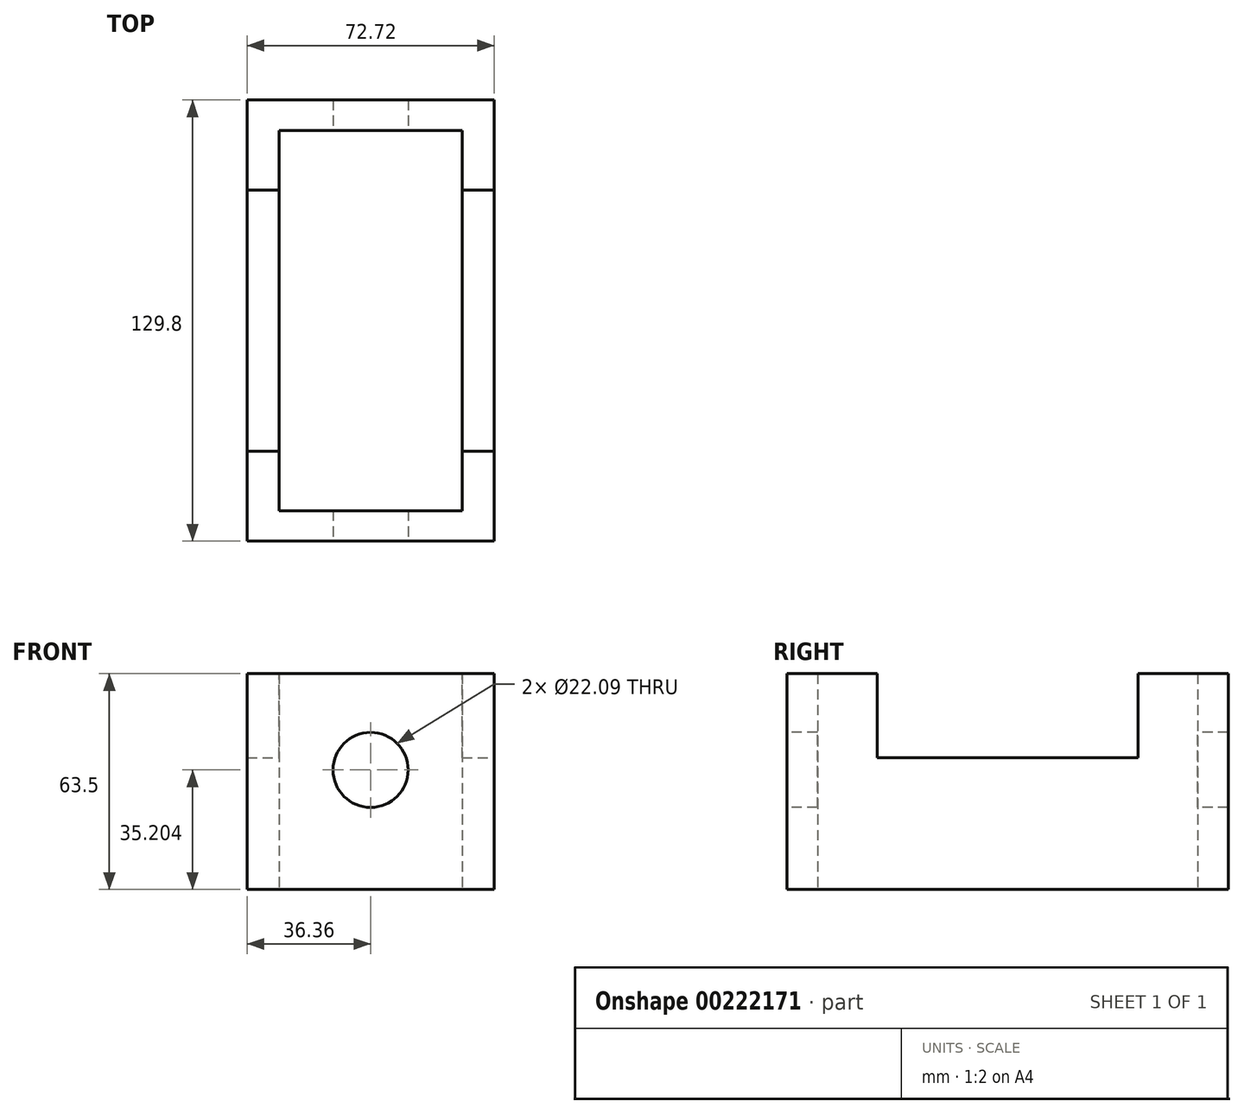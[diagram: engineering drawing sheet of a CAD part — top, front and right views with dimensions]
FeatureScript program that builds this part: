
annotation { "Feature Type Name" : "Feature", "Feature Type Description" : "" }
export const myFeature = defineFeature(function(context is Context, id is Id, definition is map)
    precondition{}
    {
        {
            var Q0;
            Q0=qCreatedBy(makeId("Top.planeOp"),FACE);
            var sketch = newSketch(context, id + "F0", { "sketchPlane" : qUnion([Q0])});
            skLineSegment(sketch, "E0.bottom", {"start": v(36.36, 64.9) * mm, "end": v(-36.36, 64.9) * mm});
            skLineSegment(sketch, "E0.top", {"start": v(36.36, -64.9) * mm, "end": v(-36.36, -64.9) * mm});
            skLineSegment(sketch, "E0.left", {"start": v(36.36, 64.9) * mm, "end": v(36.36, -64.9) * mm});
            skLineSegment(sketch, "E0.right", {"start": v(-36.36, 64.9) * mm, "end": v(-36.36, -64.9) * mm});
            skPoint(sketch, "E0.middle", {"position": v(0, 0) * mm});
            skSolve(sketch);
        }
        {
            var Q0;
            Q0 = qSketchRegion(id + "F0", true);
            extrude(context, id + "F1", {"entities" : qUnion([Q0]), "depth" : 63.5 * mm});
        }
        {
            var Q0;
            Q0=makeQuery(id+"F1.opExtrude","SWEPT_FACE",FACE,{"disambiguationData":[OSD([sQuery(id+"F0.wireOp",EDGE,"E0.top")])]});
            var sketch = newSketch(context, id + "F2", { "sketchPlane" : qUnion([Q0])});
            skCircle(sketch, "E1", {"center": v(0, 35.2) * mm, "radius": 11.05 * mm});
            skSolve(sketch);
        }
        {
            var Q0;
            Q0 = qSketchRegion(id + "F2", true);
            extrude(context, id + "F3", {"entities" : qUnion([Q0]), "operationType" : NewBodyOperationType.REMOVE, "endBound" : BoundingType.THROUGH_ALL, "oppositeDirection" : true, "depth" : 25.4 * mm});
        }
        {
            var Q0;
            Q0=makeQuery(id+"F1.opExtrude","SWEPT_FACE",FACE,{"disambiguationData":[OSD([sQuery(id+"F0.wireOp",EDGE,"E0.left")])]});
            var sketch = newSketch(context, id + "F4", { "sketchPlane" : qUnion([Q0])});
            skLineSegment(sketch, "E2.bottom", {"start": v(-38.4, 38.79) * mm, "end": v(38.4, 38.79) * mm});
            skLineSegment(sketch, "E2.top", {"start": v(-38.4, 63.88) * mm, "end": v(38.4, 63.88) * mm});
            skLineSegment(sketch, "E2.left", {"start": v(-38.4, 38.79) * mm, "end": v(-38.4, 63.88) * mm});
            skLineSegment(sketch, "E2.right", {"start": v(38.4, 38.79) * mm, "end": v(38.4, 63.88) * mm});
            skPoint(sketch, "E2.middle", {"position": v(0, 51.33) * mm});
            skSolve(sketch);
        }
        {
            var Q0;
            Q0 = qSketchRegion(id + "F4", true);
            extrude(context, id + "F5", {"entities" : qUnion([Q0]), "operationType" : NewBodyOperationType.REMOVE, "endBound" : BoundingType.THROUGH_ALL, "oppositeDirection" : true, "depth" : 25.4 * mm});
        }
        {
            var Q0;
            Q0=qCreatedBy(makeId("Top.planeOp"),FACE);
            var sketch = newSketch(context, id + "F6", { "sketchPlane" : qUnion([Q0])});
            skLineSegment(sketch, "E3.bottom", {"start": v(26.88, -55.94) * mm, "end": v(-26.88, -55.94) * mm});
            skLineSegment(sketch, "E3.top", {"start": v(26.88, 55.94) * mm, "end": v(-26.88, 55.94) * mm});
            skLineSegment(sketch, "E3.left", {"start": v(26.88, -55.94) * mm, "end": v(26.88, 55.94) * mm});
            skLineSegment(sketch, "E3.right", {"start": v(-26.88, -55.94) * mm, "end": v(-26.88, 55.94) * mm});
            skPoint(sketch, "E3.middle", {"position": v(0, 0) * mm});
            skSolve(sketch);
        }
        {
            var Q0;
            Q0 = qSketchRegion(id + "F6", true);
            extrude(context, id + "F7", {"entities" : qUnion([Q0]), "operationType" : NewBodyOperationType.REMOVE, "endBound" : BoundingType.THROUGH_ALL, "depth" : 25.4 * mm});
        }
    });
